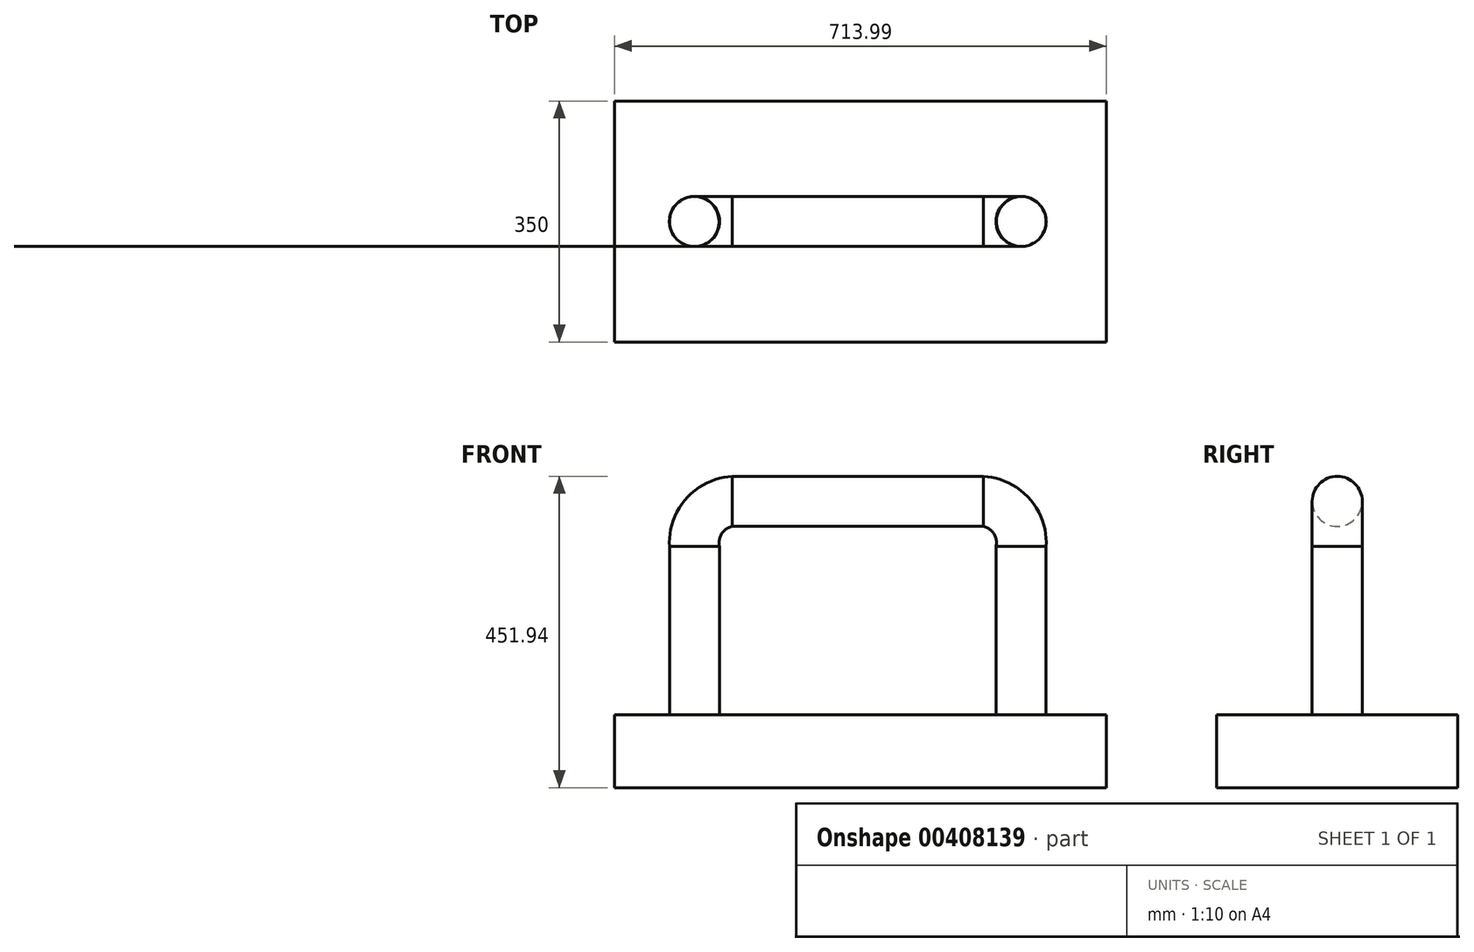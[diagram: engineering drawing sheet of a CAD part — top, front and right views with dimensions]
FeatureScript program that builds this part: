
annotation { "Feature Type Name" : "Feature", "Feature Type Description" : "" }
export const myFeature = defineFeature(function(context is Context, id is Id, definition is map)
    precondition{}
    {
        {
            var Q0;
            Q0=qCreatedBy(makeId("Top.planeOp"),FACE);
            var sketch = newSketch(context, id + "F0", { "sketchPlane" : qUnion([Q0])});
            skCircle(sketch, "E0", {"center": v(0, 0) * mm, "radius": 36.33 * mm});
            skSolve(sketch);
        }
        {
            var Q0;
            Q0=makeQuery(id+"F0.imprint","IMPRINT",FACE,{"disambiguationData":[TD([[makeQuery(id+"F0.imprint","IMPRINT",EDGE,{"derivedFrom":sQuery(id+"F0.wireOp",EDGE,"E0")}),1.0]])]});
            extrude(context, id + "F1", {"entities" : qUnion([Q0]), "depth" : 186 * mm});
        }
        {
            var Q0;
            Q0=qCreatedBy(makeId("Front.planeOp"),FACE);
            var sketch = newSketch(context, id + "F2", { "sketchPlane" : qUnion([Q0])});
            skLineSegment(sketch, "E1", {"start": v(0, 191.5) * mm, "end": v(0, 250.15) * mm});
            skLineSegment(sketch, "E2", {"start": v(-60, 310.15) * mm, "end": v(-242.47, 310.15) * mm});
            skPoint(sketch, "E3.visualSharp", {"position": v(0, 310.15) * mm});
            skArc(sketch, "E3.filletArc", {"start": v(0, 250.15) * mm, "mid": v(-17.57, 292.57) * mm, "end": v(-60, 310.15) * mm});
            skSolve(sketch);
        }
        {
            var Q0;
            Q0=makeQuery(id+"F1.opExtrude","CAP_FACE",FACE,{"disambiguationData":[OSD([sQuery(id+"F0.wireOp",EDGE,"E0")])],"isStart":false});
            var Q1;
            Q1=sQuery(id+"F2.wireOp",EDGE,"E1");
            var Q2;
            Q2=sQuery(id+"F2.wireOp",EDGE,"E3.filletArc");
            var Q3;
            Q3=sQuery(id+"F2.wireOp",EDGE,"E2");
            sweep(context, id + "F3", {"profiles" : qUnion([Q0]), "path" : qUnion([Q1, Q2, Q3])});
        }
        {
            var Q0;
            Q0=makeQuery(id+"F1.opExtrude","SWEPT_BODY",BODY,{"disambiguationData":[OSD([sQuery(id+"F0.wireOp",EDGE,"E0")])]});
            var Q1;
            Q1=makeQuery(id+"F3.opSweep","SWEPT_BODY",BODY,{"disambiguationData":[OSD([sQuery(id+"F0.wireOp",EDGE,"E0"),sQuery(id+"F2.wireOp",EDGE,"E2")])]});
            var Q2;
            Q2=makeQuery(id+"F3.opSweep","CAP_FACE",FACE,{"disambiguationData":[OSD([sQuery(id+"F0.wireOp",EDGE,"E0"),sQuery(id+"F2.wireOp",VERTEX,"E2.end")])],"isStart":false});
            mirror(context, id + "F4", {"operationType" : NewBodyOperationType.ADD, "entities" : qUnion([Q0, Q1]), "mirrorPlane" : qUnion([Q2])});
        }
        {
            var Q0;
            Q0=qCreatedBy(makeId("Front.planeOp"),FACE);
            var sketch = newSketch(context, id + "F5", { "sketchPlane" : qUnion([Q0])});
            skLineSegment(sketch, "E4.bottom", {"start": v(-590.18, 0) * mm, "end": v(123.8, 0) * mm});
            skLineSegment(sketch, "E4.top", {"start": v(-590.18, -105.47) * mm, "end": v(123.8, -105.47) * mm});
            skLineSegment(sketch, "E4.left", {"start": v(-590.18, 0) * mm, "end": v(-590.18, -105.47) * mm});
            skLineSegment(sketch, "E4.right", {"start": v(123.8, 0) * mm, "end": v(123.8, -105.47) * mm});
            skSolve(sketch);
        }
        {
            var Q0;
            Q0=makeQuery(id+"F5.imprint","IMPRINT",FACE,{"disambiguationData":[TD([[makeQuery(id+"F5.imprint","IMPRINT",EDGE,{"derivedFrom":sQuery(id+"F5.wireOp",EDGE,"E4.bottom")}),-1.0]])]});
            extrude(context, id + "F6", {"entities" : qUnion([Q0]), "depth" : 350 * mm, "symmetric" : true});
        }
    });
